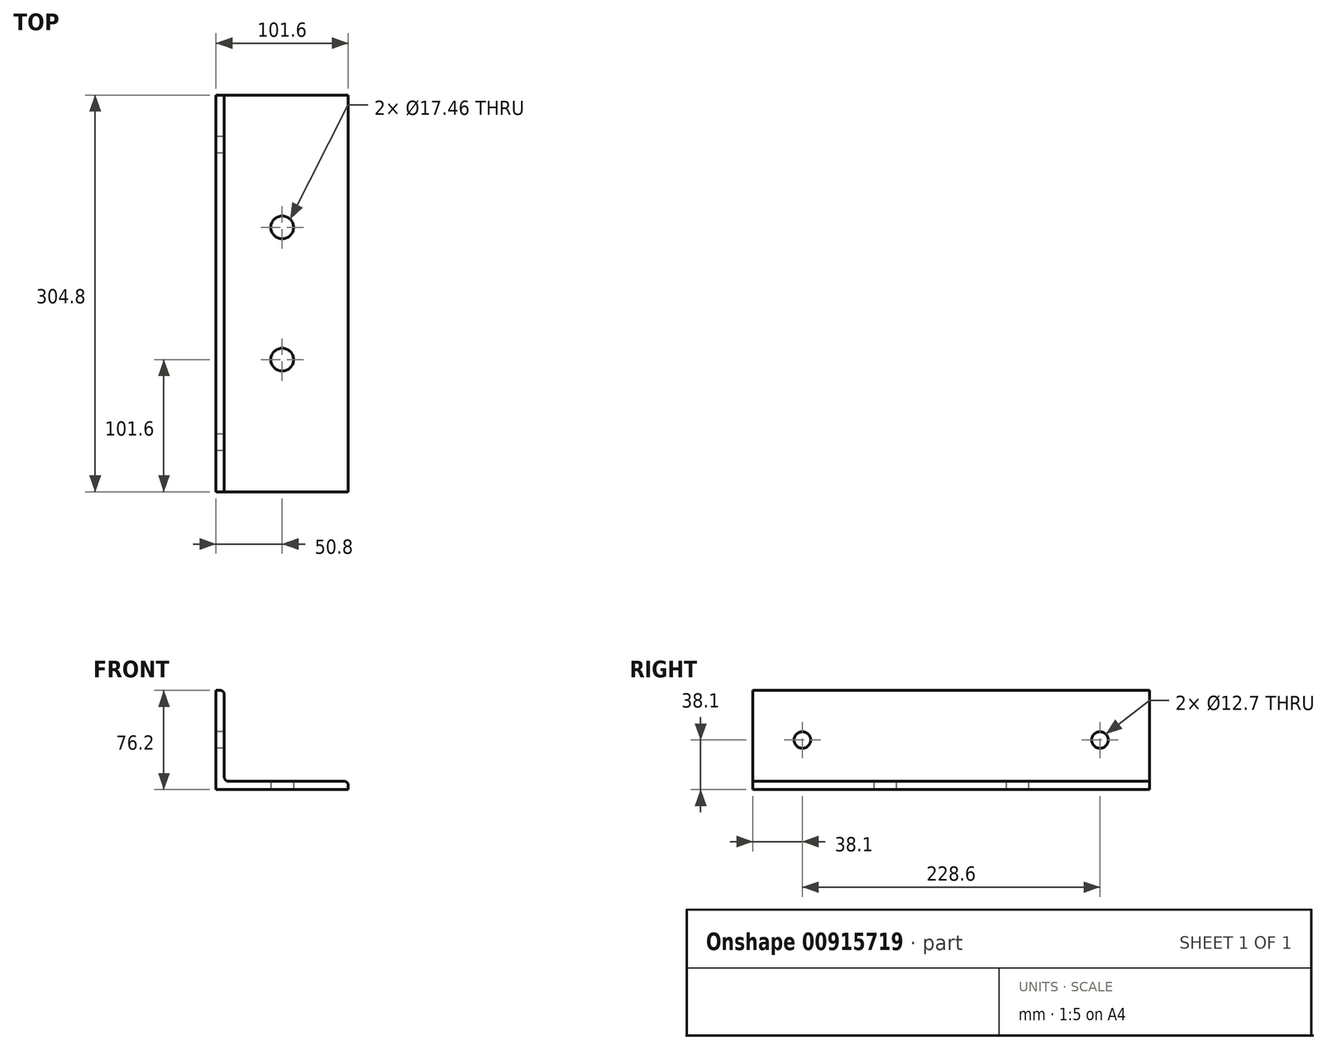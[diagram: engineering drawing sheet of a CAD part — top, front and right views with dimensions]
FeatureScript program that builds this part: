
annotation { "Feature Type Name" : "Feature", "Feature Type Description" : "" }
export const myFeature = defineFeature(function(context is Context, id is Id, definition is map)
    precondition{}
    {
        {
            var Q0;
            Q0=qCreatedBy(makeId("Front.planeOp"),FACE);
            var sketch = newSketch(context, id + "F0", { "sketchPlane" : qUnion([Q0])});
            skLineSegment(sketch, "E0", {"start": v(0, 76.2) * mm, "end": v(0, 0) * mm});
            skLineSegment(sketch, "E1", {"start": v(0, 0) * mm, "end": v(101.6, 0) * mm});
            skLineSegment(sketch, "E2", {"start": v(101.6, 0) * mm, "end": v(101.6, 3.17) * mm});
            skLineSegment(sketch, "E3", {"start": v(98.43, 6.35) * mm, "end": v(9.52, 6.35) * mm});
            skLineSegment(sketch, "E4", {"start": v(6.35, 9.52) * mm, "end": v(6.35, 73.03) * mm});
            skLineSegment(sketch, "E5", {"start": v(3.17, 76.2) * mm, "end": v(0, 76.2) * mm});
            skPoint(sketch, "E6.visualSharp", {"position": v(6.35, 6.35) * mm});
            skArc(sketch, "E6.filletArc", {"start": v(6.35, 9.52) * mm, "mid": v(7.28, 7.28) * mm, "end": v(9.52, 6.35) * mm});
            skPoint(sketch, "E7.visualSharp", {"position": v(6.35, 76.2) * mm});
            skArc(sketch, "E7.filletArc", {"start": v(6.35, 73.03) * mm, "mid": v(5.42, 75.27) * mm, "end": v(3.17, 76.2) * mm});
            skPoint(sketch, "E8.visualSharp", {"position": v(101.6, 6.35) * mm});
            skArc(sketch, "E8.filletArc", {"start": v(101.6, 3.17) * mm, "mid": v(100.67, 5.42) * mm, "end": v(98.43, 6.35) * mm});
            skSolve(sketch);
        }
        {
            var Q0;
            Q0=qSketchRegion(id+"F0",true);
            extrude(context, id + "F1", {"entities" : qUnion([Q0]), "depth" : 304.8 * mm, "offsetDistance" : 25.4 * mm, "symmetric" : true});
        }
        {
            var Q0;
            Q0=makeQuery(id+"F1.opExtrude","SWEPT_FACE",FACE,{"disambiguationData":[OSD([sQuery(id+"F0.wireOp",EDGE,"E1")])]});
            var sketch = newSketch(context, id + "F2", { "sketchPlane" : qUnion([Q0])});
            skCircle(sketch, "E9", {"center": v(50.8, 50.8) * mm, "radius": 8.73 * mm});
            skCircle(sketch, "E10", {"center": v(50.8, -50.8) * mm, "radius": 8.73 * mm});
            skLineSegment(sketch, "E11", {"start": v(0, 0) * mm, "end": v(101.6, 0) * mm, "construction": true});
            skSolve(sketch);
        }
        {
            var Q0;
            Q0=qSketchRegion(id+"F2",true);
            extrude(context, id + "F3", {"entities" : qUnion([Q0]), "operationType" : NewBodyOperationType.REMOVE, "endBound" : BoundingType.THROUGH_ALL, "oppositeDirection" : true, "depth" : 25.4 * mm, "offsetDistance" : 25.4 * mm});
        }
        {
            var Q0;
            Q0=makeQuery(id+"F1.opExtrude","SWEPT_FACE",FACE,{"disambiguationData":[OSD([sQuery(id+"F0.wireOp",EDGE,"E0")])]});
            var sketch = newSketch(context, id + "F4", { "sketchPlane" : qUnion([Q0])});
            skCircle(sketch, "E12", {"center": v(-114.3, 38.1) * mm, "radius": 6.35 * mm});
            skCircle(sketch, "E13", {"center": v(114.3, 38.1) * mm, "radius": 6.35 * mm});
            skSolve(sketch);
        }
        {
            var Q0;
            Q0=qSketchRegion(id+"F4",true);
            extrude(context, id + "F5", {"entities" : qUnion([Q0]), "operationType" : NewBodyOperationType.REMOVE, "endBound" : BoundingType.THROUGH_ALL, "oppositeDirection" : true, "depth" : 25.4 * mm, "offsetDistance" : 25.4 * mm});
        }
    });
